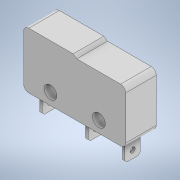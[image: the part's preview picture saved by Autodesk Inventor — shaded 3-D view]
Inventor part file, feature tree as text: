
AUTODESK INVENTOR PART (.ipt)
format: ipt  version: 2020.2 (Build 242310000, 310)  size: 174,080 bytes
history: native  units: mm
features: extrude x3, sketch x3, chamfer x1, fillet x1
ambient origin geometry x8: Origin, YZ Plane, XZ Plane, XY Plane, X Axis, Y Axis, Z Axis, Center Point
bodies: Solid1 (feature_tree)
feature tree (8):
  extrude  "Extrusion1"  Depth=11.0mm
  extrude  "Extrusion2"  Depth=10.5mm
  extrude  "Extrusion3"  Depth=1.0mm
  chamfer  "Chamfer1"  Distance=5.25mm
  fillet  "Fillet1"  Radius=6.0mm
  sketch  "Sketch1"  dims[d3=20.0mm d4=11.0mm]
  sketch  "Sketch2"  dims[d5=10.5mm d6=0.713383mm]
  sketch  "Sketch3"  dims[d7=2.5mm d8=2.25mm d9=5.25mm d10=6.0mm d11=0.0mm d12=3.0mm d13=3.0mm d14=3.0mm d15=0.5mm d16=0.5mm d17=0.5mm d18=1.65mm d19=8.5mm d20=6.7mm d21=6.0mm d22=1.5mm d23=4.0mm d24=0.0mm d25=1.0mm d26=1.5mm d27=3.0mm d28=1.5mm d29=1.65mm d30=0.0mm d31=0.4mm d32=2.0mm d33=45.0deg d34=1.0mm]
